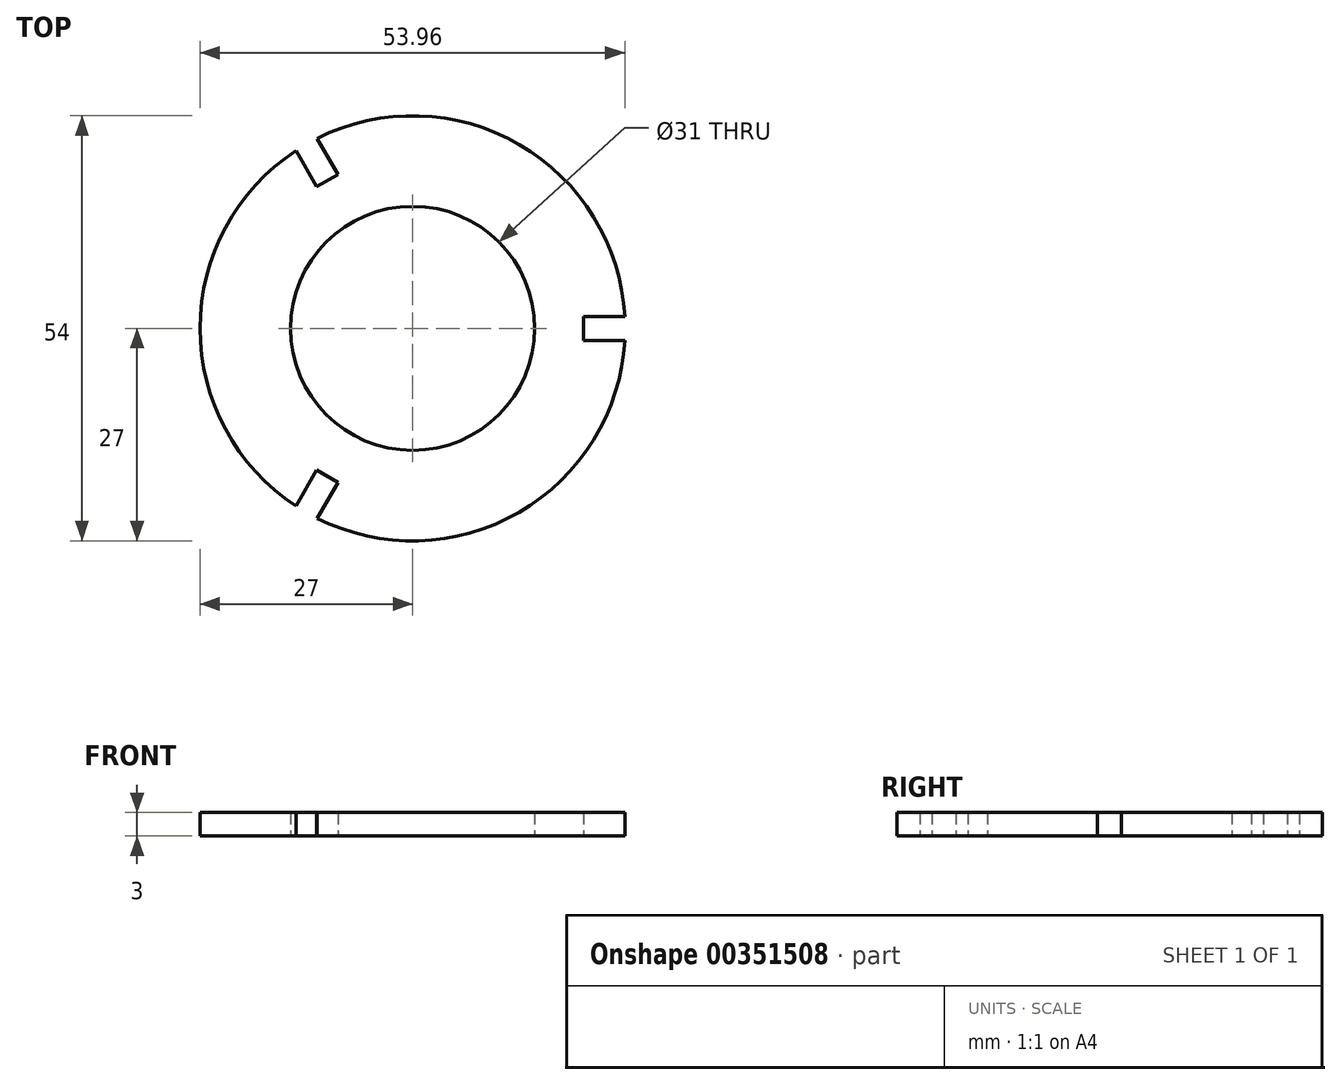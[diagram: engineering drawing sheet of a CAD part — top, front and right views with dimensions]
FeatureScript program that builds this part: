
annotation { "Feature Type Name" : "Feature", "Feature Type Description" : "" }
export const myFeature = defineFeature(function(context is Context, id is Id, definition is map)
    precondition{}
    {
        {
            var Q0;
            Q0=qCreatedBy(makeId("Top.planeOp"),FACE);
            var sketch = newSketch(context, id + "F0", { "sketchPlane" : qUnion([Q0])});
            skArc(sketch, "E0", {"start": v(-14.83, 22.56) * mm, "mid": v(-27, 0) * mm, "end": v(-14.83, -22.56) * mm});
            skCircle(sketch, "E1", {"center": v(0, 0) * mm, "radius": 15.5 * mm});
            skLineSegment(sketch, "E2", {"start": v(21.2, 1.5) * mm, "end": v(23.1, 1.5) * mm});
            skLineSegment(sketch, "E3", {"start": v(23.1, 1.5) * mm, "end": v(21.2, 1.5) * mm});
            skLineSegment(sketch, "E4", {"start": v(21.2, 1.5) * mm, "end": v(26.96, 1.5) * mm});
            skLineSegment(sketch, "E5", {"start": v(21.69, -1.56) * mm, "end": v(26.96, -1.56) * mm});
            skLineSegment(sketch, "E6", {"start": v(26.96, -1.56) * mm, "end": v(21.69, -1.56) * mm});
            skLineSegment(sketch, "E7", {"start": v(-13.13, -19.63) * mm, "end": v(-12.19, -18) * mm});
            skLineSegment(sketch, "E8", {"start": v(-12.19, -18) * mm, "end": v(-14.83, -22.56) * mm});
            skLineSegment(sketch, "E9", {"start": v(-9.49, -19.55) * mm, "end": v(-12.13, -24.12) * mm});
            skLineSegment(sketch, "E10", {"start": v(-12.13, -24.12) * mm, "end": v(-9.49, -19.55) * mm});
            skPoint(sketch, "E11.start.orphan", {"position": v(-12.2, 21.13) * mm});
            skLineSegment(sketch, "E12", {"start": v(-11.35, 22.78) * mm, "end": v(-9.5, 19.56) * mm});
            skLineSegment(sketch, "E13", {"start": v(-9.5, 19.56) * mm, "end": v(-12.13, 24.12) * mm});
            skPoint(sketch, "E14.orphan", {"position": v(-11.35, 19.78) * mm});
            skPoint(sketch, "E15.trimOffspring.end.orphan", {"position": v(-24.4, 42.27) * mm});
            skLineSegment(sketch, "E16", {"start": v(-10.88, 18.75) * mm, "end": v(-12.2, 18) * mm});
            skLineSegment(sketch, "E17", {"start": v(-12.2, 18) * mm, "end": v(-9.5, 19.56) * mm});
            skLineSegment(sketch, "E18", {"start": v(21.69, 0.02) * mm, "end": v(21.69, 1.5) * mm});
            skPoint(sketch, "E18.endSnap0", {"position": v(21.2, 1.5) * mm});
            skLineSegment(sketch, "E19", {"start": v(21.69, 1.5) * mm, "end": v(21.69, -1.56) * mm});
            skArc(sketch, "E20.trimOffspring", {"start": v(26.96, 1.5) * mm, "mid": v(13.53, 23.37) * mm, "end": v(-12.13, 24.12) * mm});
            skLineSegment(sketch, "E21", {"start": v(-12.19, -18) * mm, "end": v(-9.49, -19.55) * mm});
            skArc(sketch, "E22.trimOffspring", {"start": v(-12.13, -24.12) * mm, "mid": v(13.5, -23.38) * mm, "end": v(26.96, -1.56) * mm});
            skPoint(sketch, "E23.trimOffspring.end.orphan", {"position": v(15.43, 1.5) * mm});
            skLineSegment(sketch, "E24", {"start": v(-14.83, 22.56) * mm, "end": v(-12.2, 18) * mm});
            skLineSegment(sketch, "E25", {"start": v(-12.13, 24.12) * mm, "end": v(-9.5, 19.56) * mm});
            skLineSegment(sketch, "E26", {"start": v(21.2, 1.5) * mm, "end": v(21.69, 1.5) * mm});
            skSolve(sketch);
        }
        {
            var Q0;
            {var subQ6=sQuery(id+"F0.wireOp",EDGE,"E0");Q0=makeQuery(id+"F0.imprint","IMPRINT",FACE,{"disambiguationData":[TD([[makeQuery(id+"F0.imprint","IMPRINT",EDGE,{"derivedFrom":subQ6}),1.0]])]});}
            extrude(context, id + "F1", {"entities" : qUnion([Q0]), "depth" : 3 * mm});
        }
    });
